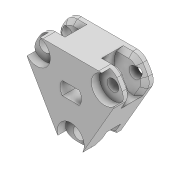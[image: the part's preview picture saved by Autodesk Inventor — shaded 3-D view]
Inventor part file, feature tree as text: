
AUTODESK INVENTOR PART (.ipt)
format: ipt  version: 2022 (Build 260153000, 153)  size: 342,528 bytes
history: native  units: mm
features: projected_geometry x7, sketch x5, extrude x4, hole x1, fillet x1, chamfer x1
ambient origin geometry x8: Origin, YZ Plane, XZ Plane, XY Plane, X Axis, Y Axis, Z Axis, Center Point
bodies: Body1 (feature_tree)
feature tree (19):
  extrude  "Extrusion3"  Depth=9.5mm
  extrude  "Extrusion4"  Depth=2.8mm
  extrude  "Extrusion5"  Depth=5.2mm
  hole  "Bohrung1"  [1 undecoded]
  extrude  "Extrusion6"  Depth=10.0mm
  fillet  "Rundung1"  Radius=10.0mm
  chamfer  "Fase1"  Distance=10.0mm
  sketch  "Skizze3"  dims[d10=22.8mm d11=9.5mm]
  sketch  "Skizze4"  dims[d12=2.8mm d13=2.8mm]
  projected_geometry  "Projizierte Kontur1"
  sketch  "Skizze6"  dims[d14=2.8mm d15=5.2mm]
  projected_geometry  "Projizierte Kontur2"
  projected_geometry  "Projizierte Kontur3"
  projected_geometry  "Projizierte Kontur4"
  projected_geometry  "Projizierte Kontur5"
  sketch  "Skizze7"  dims[d16=1.6mm d17=1.6mm]
  projected_geometry  "Projizierte Kontur6"
  sketch  "Skizze8"  dims[d18=4.0mm d19=0.0mm d20=10.0mm d21=10.0mm d22=10.0mm d23=3.3mm d24=0.0mm d25=2.0mm d26=0.0mm d27=2.8mm d28=6.0mm d29=6.5mm d30=2.0mm d31=90.0deg d32=15.0mm d33=20.594885mm d34=0.0mm d35=0.0mm d36=3.0mm d37=1.0mm d38=2.0mm d39=45.0deg]
  projected_geometry  "Projizierte Kontur7"
note: 1 required parameter value undecoded (feature->parameter linkage not recoverable at this tier; creation-order binding heuristic only, values carry confidence <= 0.55)
